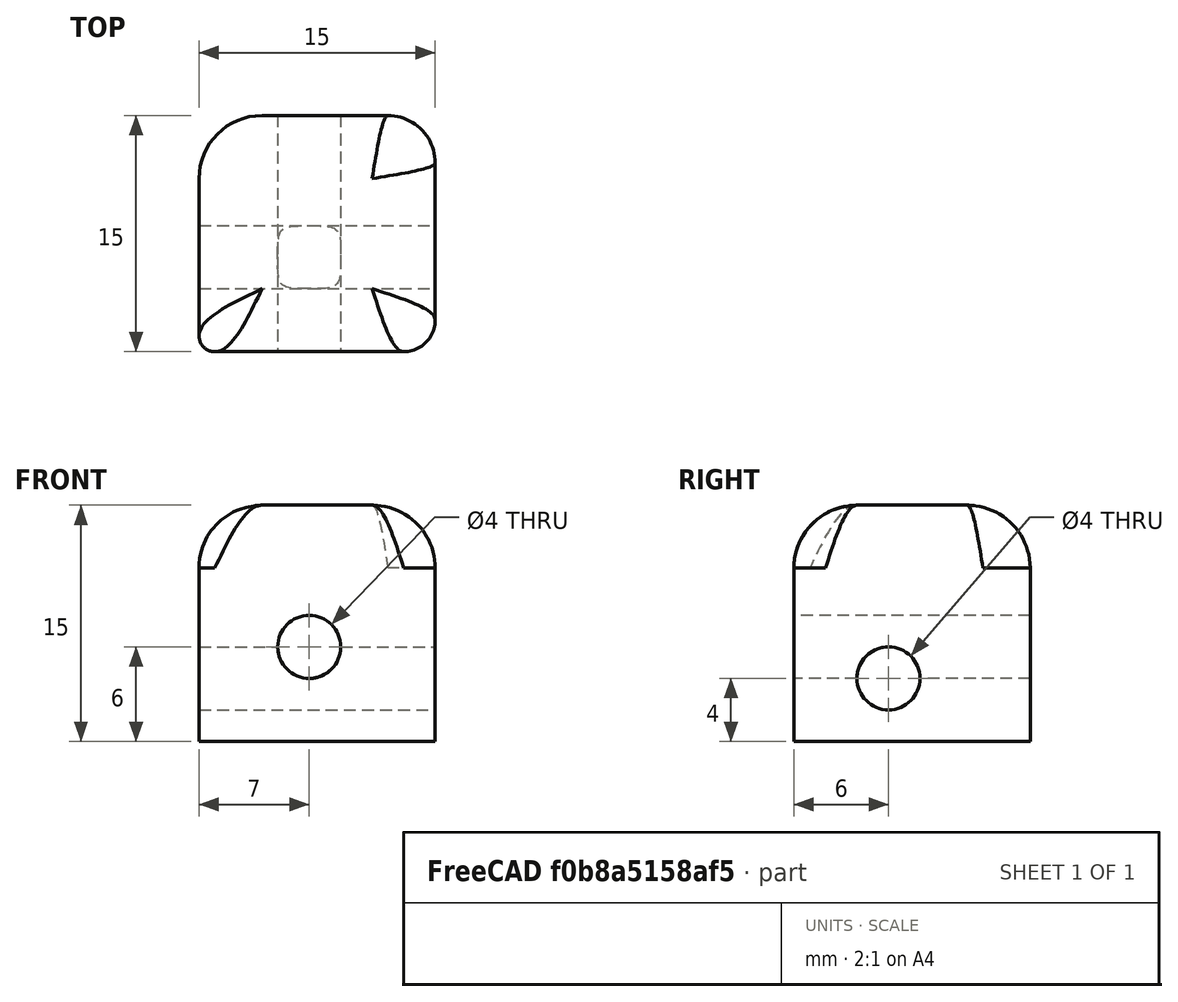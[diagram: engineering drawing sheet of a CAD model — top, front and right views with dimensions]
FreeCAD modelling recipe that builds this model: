
FCSTD DOCUMENT  (FreeCAD 0.19R)
Label: ResolutionCube
License: All rights reserved
LicenseURL: http://en.wikipedia.org/wiki/All_rights_reserved
objects: Part::Fillet×2, Part::Cylinder×2, Part::Cut×2, Part::Box×1, Mesh::Feature×1
note: 7 computed .brp shape members not serialized (recipe doc carries the construction recipe); baked Part::Feature solids carry a one-line shape summary decoded from their .brp

FEATURE [Part::Box] Box  label="Cube"
  AttacherType = Attacher::AttachEngine3D
  Height = 15
  Length = 15
  Width = 15
FEATURE [Part::Fillet] Fillet
  Base = -> Box
  Edges = 4 edges: [Edge1 r=1,Edge3 r=4,Edge5 r=2,Edge7 r=3]
FEATURE [Part::Fillet] Fillet001
  Base = -> Fillet
  Edges = 1 edges r=4: [Edge6]
FEATURE [Part::Cylinder] Cylinder
  Angle = 360
  AttacherType = Attacher::AttachEngine3D
  Height = 23
  Placement = pos=(7,19,6) rot=(1,0,0;1.5708rad)
  Radius = 2
FEATURE [Part::Cut] Cut
  Base = -> Fillet001
  Tool = -> Cylinder
FEATURE [Part::Cylinder] Cylinder001
  Angle = 360
  AttacherType = Attacher::AttachEngine3D
  Height = 21
  Placement = pos=(-1,6,4) rot=(0,1,0;1.5708rad)
  Radius = 2
FEATURE [Part::Cut] Cut001
  Base = -> Cut
  Tool = -> Cylinder001
FEATURE [Mesh::Feature] Mesh001  label="Cut001 (Meshed)001"
